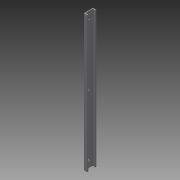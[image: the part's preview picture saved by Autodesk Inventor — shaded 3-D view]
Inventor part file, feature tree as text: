
AUTODESK INVENTOR PART (.ipt)
format: ipt  version: 2014 SP2 (Build 180246200, 246)  size: 111,616 bytes
history: native  units: mm
features: other x21, sketch x2, extrude x1, revolve x1, pattern_linear x1
ambient origin geometry x8: Origin, YZ Plane, XZ Plane, XY Plane, X Axis, Y Axis, Z Axis, Center Point
bodies: Solid1 (feature_tree)
feature tree (26):
  extrude  "Extrusion1"  TaperAngle=360.0deg  [1 undecoded]
  revolve  "Revolution1"  [1 undecoded]
  pattern_linear  "Rectangular Pattern1"  [2 undecoded]
  other  "to_ball_XY"
  other  "to_ball_YZ"
  other  "to_ball_ZX"
  other  "to_ball_X"
  other  "to_ball_Y"
  other  "to_ball_Z"
  other  "to_ball_Center"
  other  "to_ball1_XY"
  other  "to_ball1_YZ"
  other  "to_ball1_ZX"
  other  "to_ball1_X"
  other  "to_ball1_Y"
  other  "to_ball1_Z"
  other  "to_ball1_Center"
  other  "to_rail_XY"
  other  "to_rail_YZ"
  other  "to_rail_ZX"
  other  "to_rail_X"
  other  "to_rail_Y"
  other  "to_rail_Z"
  other  "to_rail_Center"
  sketch  "Sketch_1"  dims[d0=300.0mm d1=0.0mm d2=360.0deg]
  sketch  "Sketch_2"  dims[d3=30.0mm d5=135.0mm d6=10.0mm d8=0.0mm]
note: 4 required parameter values undecoded (feature->parameter linkage not recoverable at this tier; creation-order binding heuristic only, values carry confidence <= 0.55)
